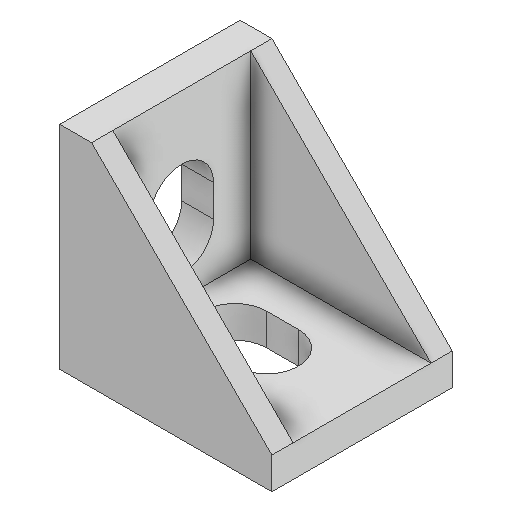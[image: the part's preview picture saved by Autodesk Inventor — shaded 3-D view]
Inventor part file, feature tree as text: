
AUTODESK INVENTOR PART (.ipt)
format: ipt  version: 2024.1 (Build 281209000, 209)  size: 134,144 bytes
history: native  units: in
note: dims shown in document units (in); Inventor stores cm internally (conversion verified against a paired STEP export)
features: other x3, sketch x2, plane x1
ambient origin geometry x8: Origin, YZ Plane, XZ Plane, XY Plane, X Axis, Y Axis, Z Axis, Center Point
bodies: Solid1 (feature_tree)
feature tree (6):
  other  "20x20 90 Gusset.ipt"
  other  "Solid1::20x20 90 Gusset.ipt"
  other  "TaggingFeature1"
  sketch  "Sketch3"  dims[d0=0.3937in]
  sketch  "Sketch4"
  plane  "Work Plane1"
